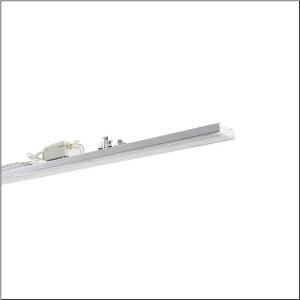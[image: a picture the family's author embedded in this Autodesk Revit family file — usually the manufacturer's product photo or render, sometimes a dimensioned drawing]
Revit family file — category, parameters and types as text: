
# Revit family: licross_r__21_recessed_ho_52tl12dn4fxm3s4_75bd
name_source: partatom
category: Lighting Fixtures
units: mm (PartAtom-declared; Revit-internal decimal feet)

## family parameters
Cut with Voids When Loaded = No
Host = Face
Light Source = No
Part Type = Normal
Room Calculation Point = No
Round Connector Dimension = Use Diameter
Shared = No

## types (1)
- --- (1 x LED, 930 lm, 7.5 W, 4000K)
    Apparent Load = 8 VA
    CIE Flux Codes = 69 91 98 100 100
    Color Rendering = 80
    Color Temperature = 4000K
    Default Elevation = 1800 mm
    Description = Licross® 21 Recessed HO, luminaire insert, of sheet steel, galvanised, coil coated, white, length: 1.500mm, width: 66mm, height: 67mm, LED rated luminous flux: 15.000lm, light colour: 840, control gear: DALI 2, with plug, 6-pole, with phase selection, for trunking rail, 9 or 11-core, mains connection: 220..240V, AC, 50/60Hz, rated input power: 88W, halogen-free wiring, for emergency light function, for trunking rail, 9-/11-core, converter,control gear: single battery element, battery: LiFeP04, 9Ah, primary optical cover: cover, of PMMA, light emission: direct distribution, primary light characteristic: symmetric, protection rating (complete): IP40, insulation class (complete): insulation class I (protective earthing), certification: CE, UKCA, protection symbol: D if used in an environment without relevant dust loads with corresponding accessories, impact resistance: IK06, permissible ambient temperature for indoor applications: +5..+35°C, standard: EN 60598-2-22, LABS conformity tested according to VDMA 24364:2018-05, reducing of maximum allowable ambient temperature of 5°C with ceiling mounting, corresponds to IFS (International Featured Standards) requirements for safety and quality in the food industry, packaging unit: 1 piece
    Height = 58 mm
    Lamp = 1 x LED
    Lamp Light Flux = 930 lm
    Lamp Power = 7.5 W
    Lamp count = 1
    Length = 1500 mm
    Luminous efficacy = 124 lm/W
    Manufacturer = Siteco
    ModVariant = No
    Model = 52TL12DN4FXM3S4
    Mounting Place = Ceiling
    Mounting Type = Pendant
    Number of Poles = 1
    OnlyDefault = Yes
    Power Factor = 1
    Product Name = Licross® 21 Recessed HO
    Product group = luminaire insert
    ProductGroupID = 901
    Protection Class = Protection class I
    Protection Degree = IP 40
    RLX_Detail_Level = 1
    RLX_Emergency_Light_Flux = 0 lm
    RLX_Emergency_Type = 0
    RLX_Emergency_Type_DB = No
    RlxData = <blob elided: 25121 chars, md5=6d7ac601>
    Socket = socket
    Standby Power = 0 W
    System Light Flux = 930 lm
    System Power = 8 W
    Type Comments = : emergency light operation: 3 h
    Type Image = l_1296930.jpg
    URL = http://relux.com
    VarID = @adj_039443
    Voltage = 0 V
    Weight = 0.00 kg
    Width = 66 mm

## geometry (parser evidence)
native form markers: Blend x4, Sweep x11
no freeform markers — native parametric forms only
